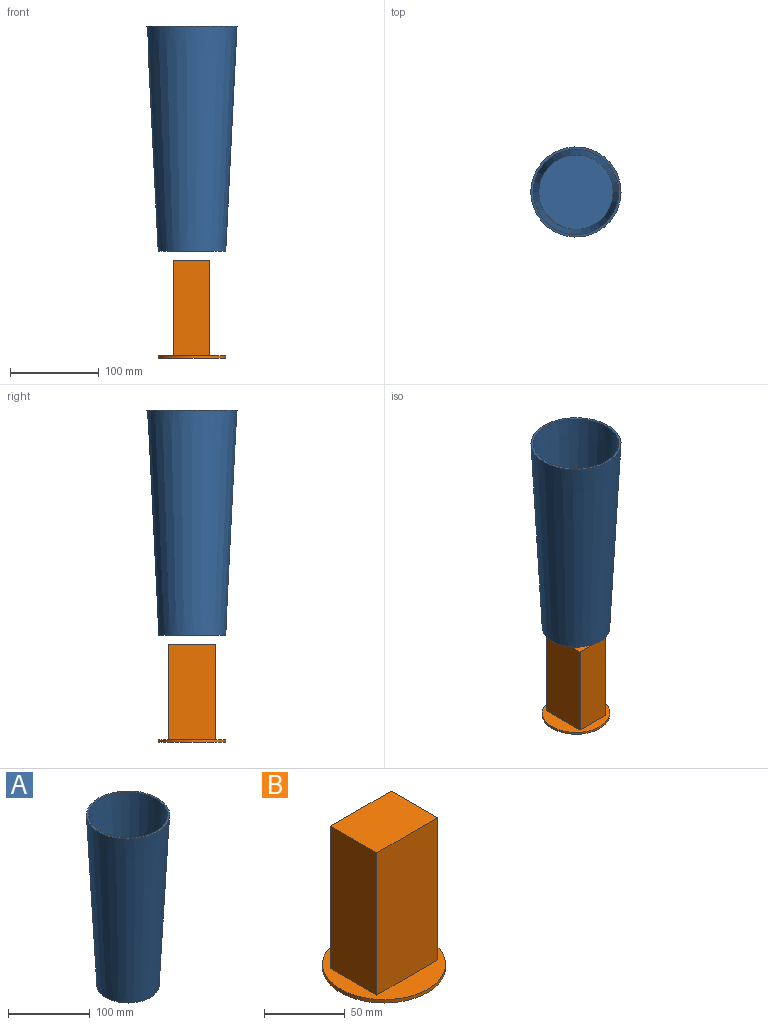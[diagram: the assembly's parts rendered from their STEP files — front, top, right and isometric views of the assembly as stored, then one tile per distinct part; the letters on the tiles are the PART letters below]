
ASSEMBLY  parts=2 mates=1
PART A: 15 faces, bbox 101.6x101.6x254 mm
  f0: cone r=35.56mm half-angle=2.9deg, axis (0,0,1), area 29707.4mm2, adj f2,f3,f4,f8,f9,f10,f11,f12
  f1: plane 76.2x76.2mm, normal (0,0,-1), area 2076.5mm2, adj f7,f9,f10,f11,f12
  f2: plane 44.39x7.74mm, normal (0,0,1), area 234.7mm2, adj f0,f9
  f3: plane 55.84x13.46mm, normal (0,0,1), area 523.5mm2, adj f0,f10
  f4: plane 44.39x7.74mm, normal (0,0,1), area 234.7mm2, adj f0,f11
  f5: cone r=35.56mm half-angle=2.9deg, axis (0,0,1), area 36018.6mm2, adj f6,f13
  f6: plane 101.6x101.6mm, normal (0,0,1), area 791.4mm2, adj f5,f7
  f7: cone r=38.1mm half-angle=2.9deg, axis (0,0,1), area 71027.7mm2, adj f1,f6
  f8: plane 55.84x13.46mm, normal (0,0,1), area 523.5mm2, adj f0,f12
  f9: plane 44.45x2.89mm, normal (0,-1,0), area 112.9mm2, adj f0,f1,f2,f10,f12
  f10: plane 55.88x2.89mm, normal (-1,0,0), area 141.9mm2, adj f0,f1,f3,f9,f11
  f11: plane 44.45x2.89mm, normal (0,1,0), area 112.9mm2, adj f0,f1,f4,f10,f12
  f12: plane 55.88x2.89mm, normal (1,0,0), area 141.9mm2, adj f0,f1,f8,f9,f11
  f13: plane 83.81x83.81mm, normal (0,0,1), area 5517.2mm2, adj f5
  f14: plane 83.56x83.56mm, normal (0,0,-1), area 5483.8mm2, adj f0
PART B: 8 faces, bbox 76.2x76.2x110.5 mm
  f0: plane 107.95x53.34mm, normal (0,-1,0), area 5758.1mm2, adj f1,f3,f4,f5
  f1: plane 107.95x40.64mm, normal (1,0,0), area 4387.1mm2, adj f0,f2,f4,f5
  f2: plane 107.95x53.34mm, normal (0,1,0), area 5758.1mm2, adj f1,f3,f4,f5
  f3: plane 107.95x40.64mm, normal (-1,0,0), area 4387.1mm2, adj f0,f2,f4,f5
  f4: plane 53.34x40.64mm, normal (0,0,1), area 2167.7mm2, adj f0,f1,f2,f3
  f5: plane 76.2x76.2mm, normal (0,0,1), area 2392.6mm2, adj f0,f1,f2,f3,f6
  f6: cylinder r=38.1mm len=76.2mm, axis (0,0,1), area 608mm2, adj f5,f7
  f7: plane 76.2x76.2mm, normal (0,0,-1), area 4560.4mm2, adj f6
PLACE A at identity fixed
PLACE B rot(axis=(0,0,-1),90deg) t=(0,0,-117.81)mm
MATE slider B.f6 <-> A.f0  axis (0,0,1) through (0,0,-117.81)mm
